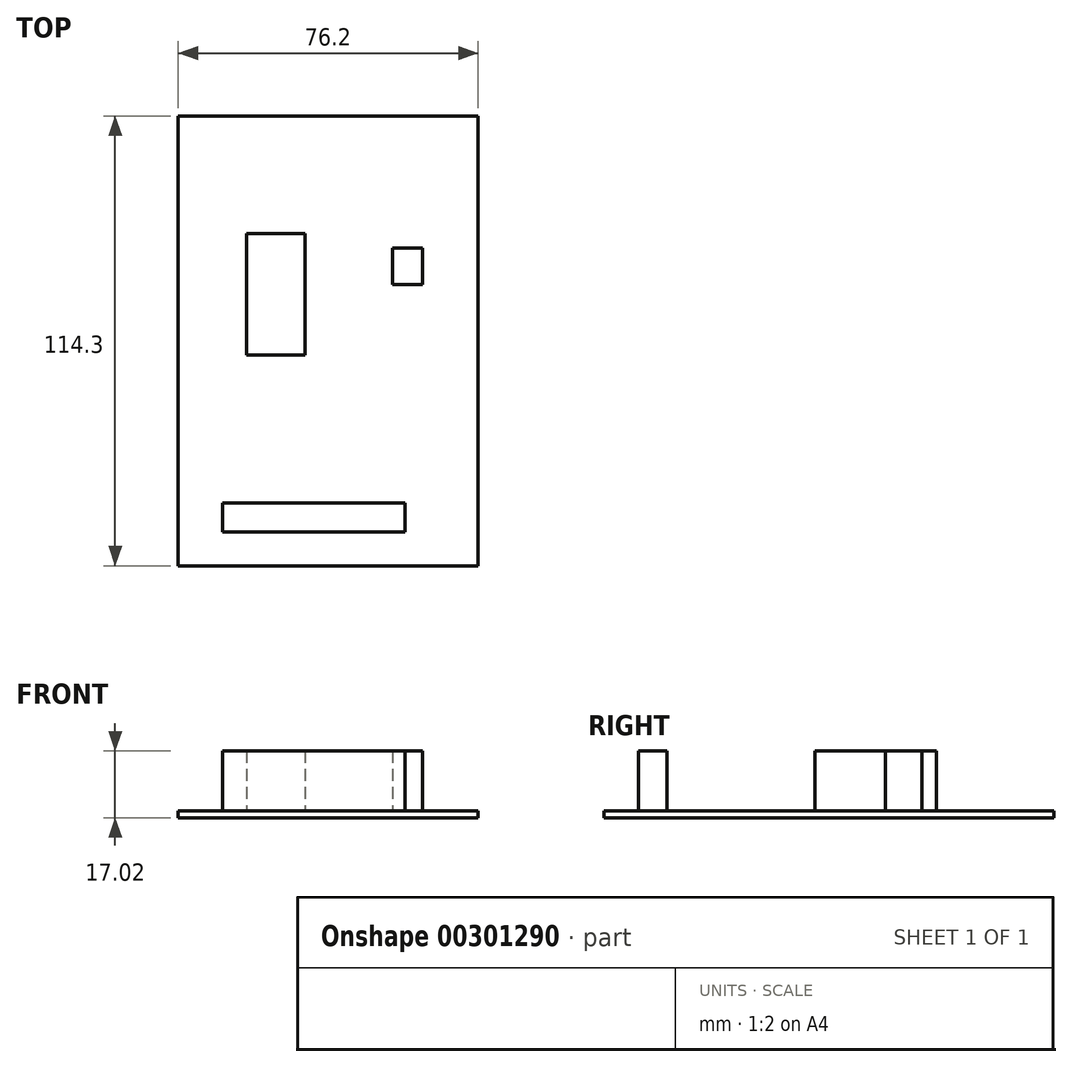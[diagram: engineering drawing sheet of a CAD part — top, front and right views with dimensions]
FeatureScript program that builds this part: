
annotation { "Feature Type Name" : "Feature", "Feature Type Description" : "" }
export const myFeature = defineFeature(function(context is Context, id is Id, definition is map)
    precondition{}
    {
        {
            var Q0;
            Q0=qCreatedBy(makeId("Top.planeOp"),FACE);
            var sketch = newSketch(context, id + "F0", { "sketchPlane" : qUnion([Q0])});
            skLineSegment(sketch, "E0.bottom", {"start": v(0, 0) * mm, "end": v(76.2, 0) * mm});
            skLineSegment(sketch, "E0.top", {"start": v(0, 114.3) * mm, "end": v(76.2, 114.3) * mm});
            skLineSegment(sketch, "E0.left", {"start": v(0, 0) * mm, "end": v(0, 114.3) * mm});
            skLineSegment(sketch, "E0.right", {"start": v(76.2, 0) * mm, "end": v(76.2, 114.3) * mm});
            skSolve(sketch);
        }
        {
            var Q0;
            Q0 = qSketchRegion(id + "F0", true);
            extrude(context, id + "F1", {"entities" : qUnion([Q0]), "depth" : 1.78 * mm});
        }
        {
            var Q0;
            Q0=makeQuery(id+"F1.opExtrude","CAP_FACE",FACE,{"disambiguationData":[OSD([sQuery(id+"F0.wireOp",EDGE,"E0.bottom"),sQuery(id+"F0.wireOp",EDGE,"E0.top"),sQuery(id+"F0.wireOp",EDGE,"E0.left"),sQuery(id+"F0.wireOp",EDGE,"E0.right")])],"isStart":false});
            var sketch = newSketch(context, id + "F2", { "sketchPlane" : qUnion([Q0])});
            skLineSegment(sketch, "E1.bottom", {"start": v(11.23, 8.67) * mm, "end": v(57.64, 8.67) * mm});
            skLineSegment(sketch, "E1.top", {"start": v(11.23, 16) * mm, "end": v(57.64, 16) * mm});
            skLineSegment(sketch, "E1.left", {"start": v(11.23, 8.67) * mm, "end": v(11.23, 16) * mm});
            skLineSegment(sketch, "E1.right", {"start": v(57.64, 8.67) * mm, "end": v(57.64, 16) * mm});
            skLineSegment(sketch, "E2.bottom", {"start": v(17.34, 84.38) * mm, "end": v(32.24, 84.38) * mm});
            skLineSegment(sketch, "E2.top", {"start": v(17.34, 53.6) * mm, "end": v(32.24, 53.6) * mm});
            skLineSegment(sketch, "E2.left", {"start": v(17.34, 84.38) * mm, "end": v(17.34, 53.6) * mm});
            skLineSegment(sketch, "E2.right", {"start": v(32.24, 84.38) * mm, "end": v(32.24, 53.6) * mm});
            skLineSegment(sketch, "E3.bottom", {"start": v(62.03, 80.72) * mm, "end": v(54.46, 80.72) * mm});
            skLineSegment(sketch, "E3.top", {"start": v(62.03, 71.44) * mm, "end": v(54.46, 71.44) * mm});
            skLineSegment(sketch, "E3.left", {"start": v(62.03, 80.72) * mm, "end": v(62.03, 71.44) * mm});
            skLineSegment(sketch, "E3.right", {"start": v(54.46, 80.72) * mm, "end": v(54.46, 71.44) * mm});
            skSolve(sketch);
        }
        {
            var Q0;
            Q0 = qSketchRegion(id + "F2", true);
            extrude(context, id + "F3", {"entities" : qUnion([Q0]), "operationType" : NewBodyOperationType.ADD, "depth" : 15.24 * mm});
        }
    });
